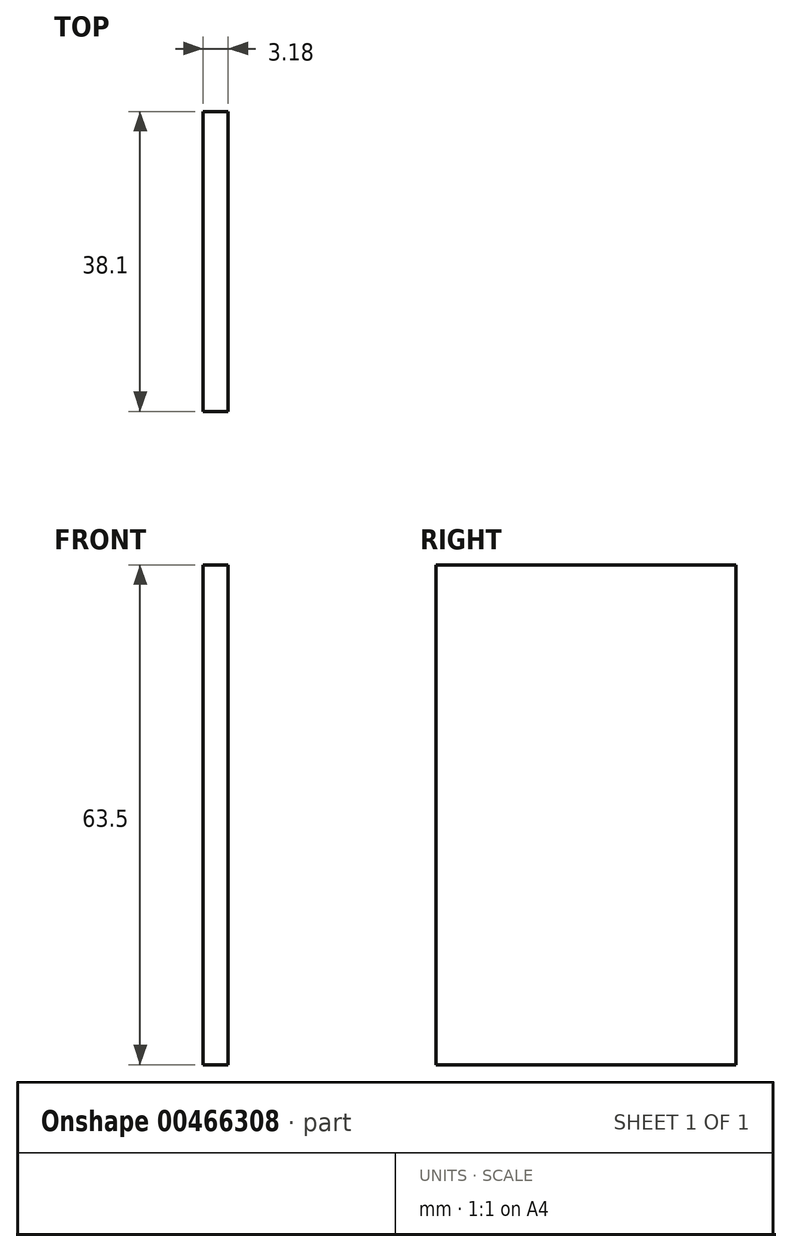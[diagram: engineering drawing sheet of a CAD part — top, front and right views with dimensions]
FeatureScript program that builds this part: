
annotation { "Feature Type Name" : "Feature", "Feature Type Description" : "" }
export const myFeature = defineFeature(function(context is Context, id is Id, definition is map)
    precondition{}
    {
        {
            var Q0;
            Q0=qCreatedBy(makeId("Front.planeOp"),FACE);
            var sketch = newSketch(context, id + "F0", { "sketchPlane" : qUnion([Q0])});
            skLineSegment(sketch, "E0", {"start": v(-45.8, 1.57) * mm, "end": v(-45.8, -61.93) * mm});
            skLineSegment(sketch, "E1", {"start": v(-45.8, -61.93) * mm, "end": v(-48.97, -61.93) * mm});
            skLineSegment(sketch, "E2", {"start": v(-48.97, 1.57) * mm, "end": v(-48.97, -61.93) * mm});
            skLineSegment(sketch, "E3", {"start": v(-45.8, 1.57) * mm, "end": v(-48.97, 1.57) * mm});
            skSolve(sketch);
        }
        {
            var Q0;
            Q0=makeQuery(id+"F0.imprint","IMPRINT",FACE,{"disambiguationData":[TD([[makeQuery(id+"F0.imprint","IMPRINT",EDGE,{"derivedFrom":sQuery(id+"F0.wireOp",EDGE,"E0")}),-1.0]])]});
            extrude(context, id + "F1", {"entities" : qUnion([Q0]), "depth" : 38.1 * mm});
        }
    });
